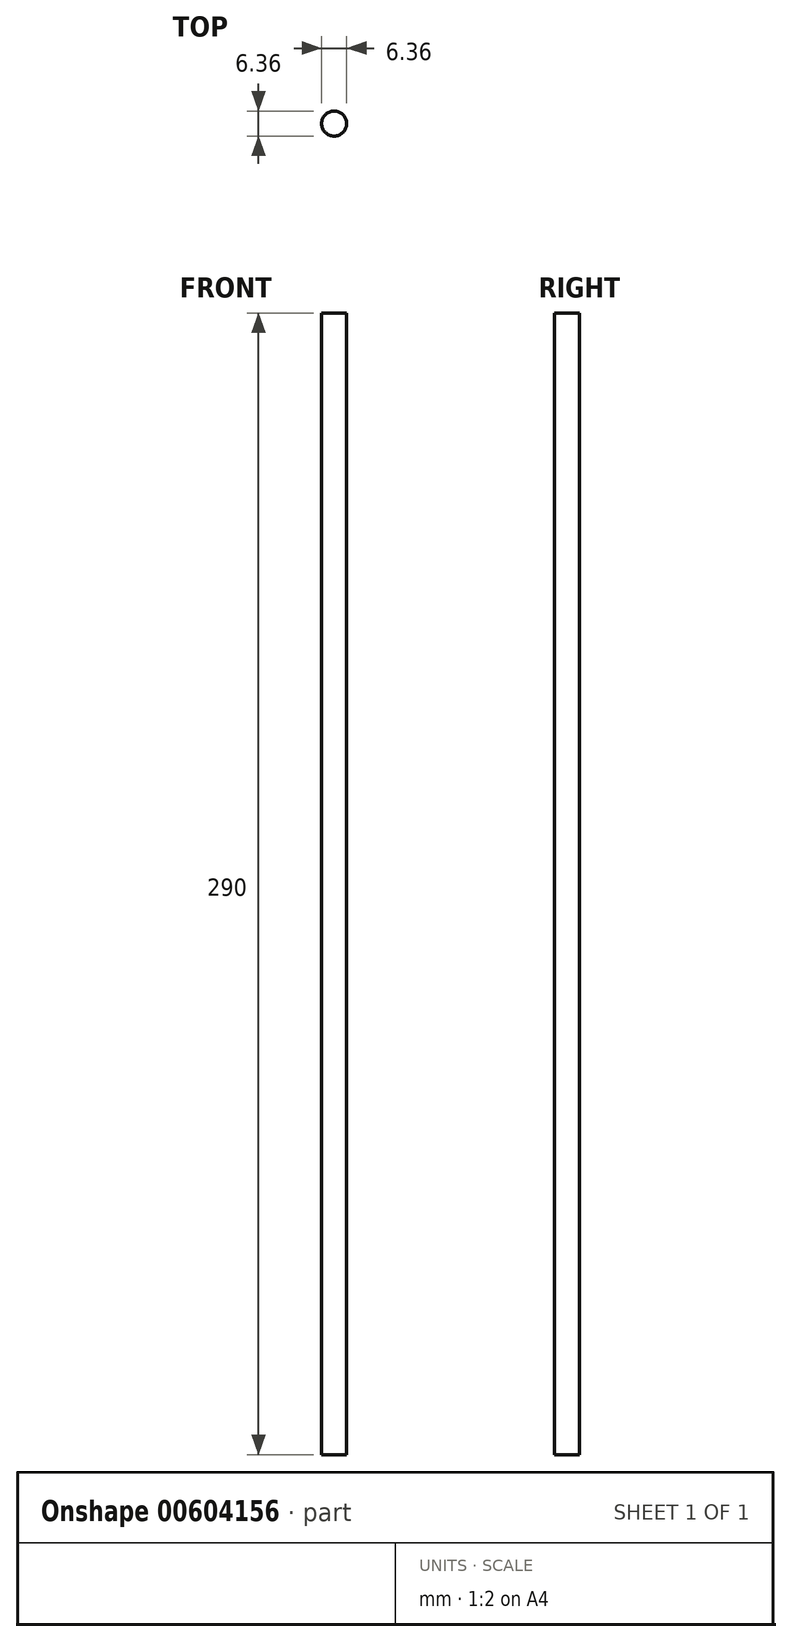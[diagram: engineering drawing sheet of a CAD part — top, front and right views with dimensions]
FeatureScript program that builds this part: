
annotation { "Feature Type Name" : "Feature", "Feature Type Description" : "" }
export const myFeature = defineFeature(function(context is Context, id is Id, definition is map)
    precondition{}
    {
        {
            var Q0;
            Q0=qCreatedBy(makeId("Top.planeOp"),FACE);
            var sketch = newSketch(context, id + "F0", { "sketchPlane" : qUnion([Q0])});
            skCircle(sketch, "E0", {"center": v(0, 0) * mm, "radius": 3.18 * mm});
            skSolve(sketch);
        }
        {
            var Q0;
            Q0=makeQuery(id+"F0.imprint","IMPRINT",FACE,{"disambiguationData":[TD([[makeQuery(id+"F0.imprint","IMPRINT",EDGE,{"derivedFrom":sQuery(id+"F0.wireOp",EDGE,"E0")}),1.0]])]});
            extrude(context, id + "F1", {"entities" : qUnion([Q0]), "depth" : 290 * mm, "offsetDistance" : 25 * mm});
        }
    });
